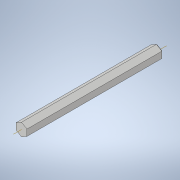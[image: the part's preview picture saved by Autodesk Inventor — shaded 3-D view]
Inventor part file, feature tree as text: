
AUTODESK INVENTOR PART (.ipt)
format: ipt  version: 2021 (Build 250183000, 183)  size: 121,856 bytes
history: native  units: in
note: dims shown in document units (in); Inventor stores cm internally (conversion verified against a paired STEP export)
features: sketch x2, extrude x1, other x1
ambient origin geometry x8: Origin, YZ Plane, XZ Plane, XY Plane, X Axis, Y Axis, Z Axis, Center Point
bodies: Solid2 (feature_tree), Solid1 (feature_tree)
feature tree (4):
  extrude  "Extrusion1"  [1 undecoded]
  sketch  "Sketch2"
  other  "Work Axis1"
  sketch  "Sketch1"  dims[d0=2.875in d1=0.0in]
note: 1 required parameter value undecoded (feature->parameter linkage not recoverable at this tier; creation-order binding heuristic only, values carry confidence <= 0.55)
